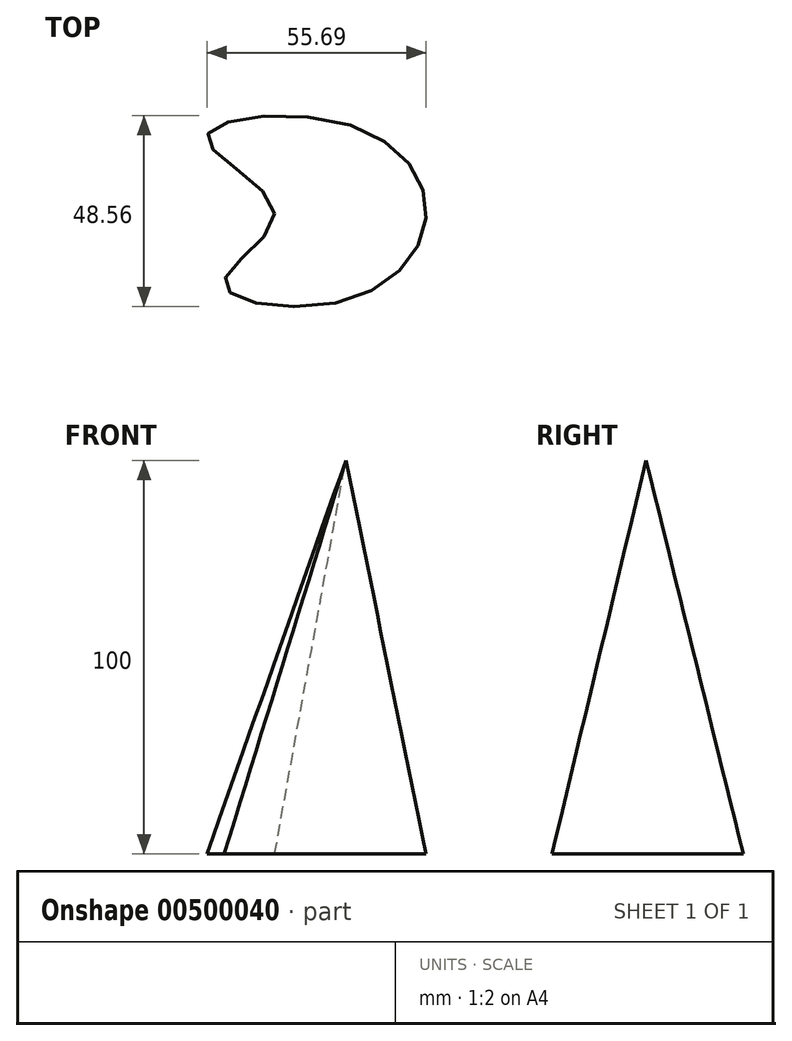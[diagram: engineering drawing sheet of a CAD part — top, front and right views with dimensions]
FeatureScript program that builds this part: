
annotation { "Feature Type Name" : "Feature", "Feature Type Description" : "" }
export const myFeature = defineFeature(function(context is Context, id is Id, definition is map)
    precondition{}
    {
        {
            var Q0;
            Q0=qCreatedBy(makeId("Top.planeOp"),FACE);
            var sketch = newSketch(context, id + "F0", { "sketchPlane" : qUnion([Q0])});
            skFitSpline(sketch, "E0", {"points": [v(0, 22.59) * mm, v(20.4, 0) * mm, v(0, -22.3) * mm, v(-30.9, -17.63) * mm, v(-18.07, 0) * mm, v(-35.27, 18.8) * mm, v(0, 22.59) * mm]});
            skSolve(sketch);
        }
        {
            var Q0;
            Q0=qCreatedBy(makeId("Top.planeOp"),FACE);
            cPlane(context, id + "F1", {"entities" : qUnion([Q0]), "cplaneType" : CPlaneType.OFFSET, "offset" : 100 * mm, "width" : 152.4 * mm, "height" : 152.4 * mm});
        }
        {
            var Q0;
            Q0=qCreatedBy(id+"F1.planeOp",FACE);
            var sketch = newSketch(context, id + "F2", { "sketchPlane" : qUnion([Q0])});
            skPoint(sketch, "E1", {"position": v(0, 0) * mm});
            skSolve(sketch);
        }
        {
            var Q0;
            Q0=makeQuery(id+"F0.imprint","IMPRINT",FACE,{"disambiguationData":[TD([[makeQuery(id+"F0.imprint","IMPRINT",EDGE,{"derivedFrom":sQuery(id+"F0.wireOp",EDGE,"E0")}),-1.0]])]});
            var Q1;
            Q1=sQuery(id+"F2.wireOp",VERTEX,"E1");
            loft(context, id + "F3", {"sheetProfilesArray" : [{ "sheetProfileEntities" : qUnion([Q0]) }, { "sheetProfileEntities" : qUnion([Q1]) }]});
        }
    });
